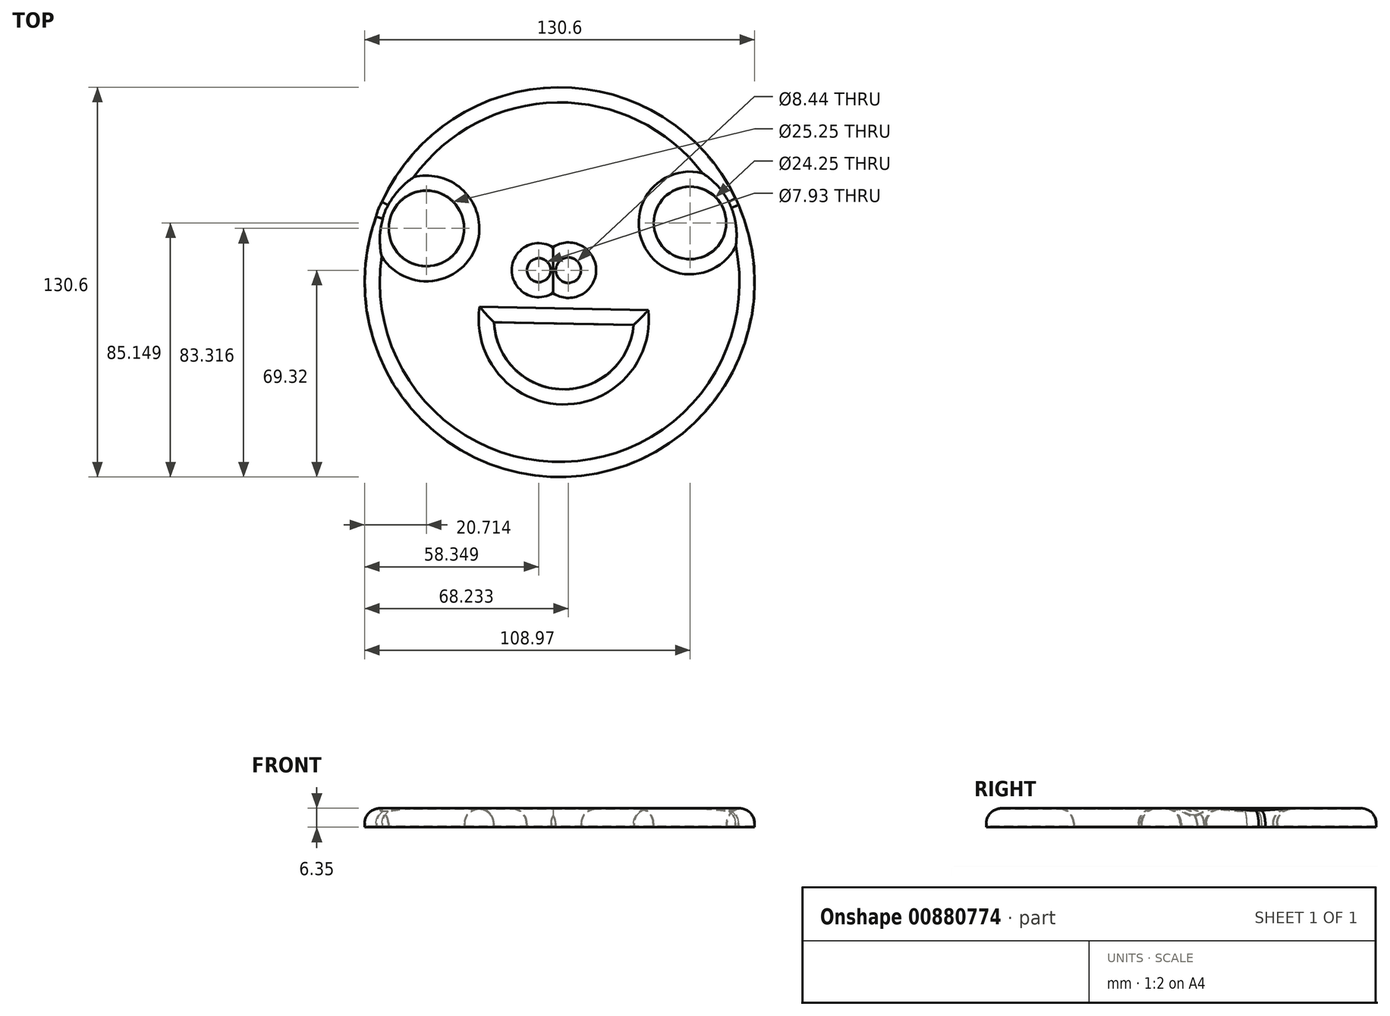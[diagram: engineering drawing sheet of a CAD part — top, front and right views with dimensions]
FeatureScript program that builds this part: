
annotation { "Feature Type Name" : "Feature", "Feature Type Description" : "" }
export const myFeature = defineFeature(function(context is Context, id is Id, definition is map)
    precondition{}
    {
        {
            var Q0;
            Q0=qCreatedBy(makeId("Top.planeOp"),FACE);
            var sketch = newSketch(context, id + "F0", { "sketchPlane" : qUnion([Q0])});
            skCircle(sketch, "E0", {"center": v(43.67, 24.89) * mm, "radius": 17.36 * mm});
            skCircle(sketch, "E1", {"center": v(-44.59, 23.06) * mm, "radius": 17.36 * mm});
            skCircle(sketch, "E2", {"center": v(-44.59, 23.06) * mm, "radius": 12.62 * mm});
            skCircle(sketch, "E3", {"center": v(43.67, 24.89) * mm, "radius": 12.12 * mm});
            skCircle(sketch, "E4", {"center": v(0, 5.04) * mm, "radius": 65.3 * mm});
            skArc(sketch, "E5", {"start": v(-21.99, -8.4) * mm, "mid": v(0.94, -30.84) * mm, "end": v(24.74, -9.31) * mm});
            skLineSegment(sketch, "E6", {"start": v(-21.99, -8.4) * mm, "end": v(24.74, -9.31) * mm});
            skCircle(sketch, "E7", {"center": v(-6.95, 9.06) * mm, "radius": 3.97 * mm});
            skCircle(sketch, "E8", {"center": v(2.93, 9.06) * mm, "radius": 4.22 * mm});
            skSolve(sketch);
        }
        {
            var Q0;
            Q0 = qSketchRegion(id + "F0", true);
            extrude(context, id + "F1", {"entities" : qUnion([Q0]), "depth" : 6.35 * mm, "offsetDistance" : 25.4 * mm});
        }
        {
            var Q0;
            Q0=makeQuery(id+"F1.opExtrude","CAP_FACE",FACE,{"disambiguationData":[OSD([sQuery(id+"F0.wireOp",EDGE,"E0"),sQuery(id+"F0.wireOp",EDGE,"E1"),sQuery(id+"F0.wireOp",EDGE,"E2"),sQuery(id+"F0.wireOp",EDGE,"E3"),sQuery(id+"F0.wireOp",EDGE,"E4"),sQuery(id+"F0.wireOp",EDGE,"E5"),sQuery(id+"F0.wireOp",EDGE,"E6")])],"isStart":false});
            fillet(context, id + "F2", {"entities" : qUnion([Q0]), "radius" : 5.08 * mm, "tangentPropagation" : true, "allowEdgeOverflow" : false});
        }
        {
            var Q0;
            Q0=makeQuery(id+"F1.opExtrude","CAP_FACE",FACE,{"disambiguationData":[OSD([sQuery(id+"F0.wireOp",EDGE,"E0"),sQuery(id+"F0.wireOp",EDGE,"E1"),sQuery(id+"F0.wireOp",EDGE,"E2"),sQuery(id+"F0.wireOp",EDGE,"E3"),sQuery(id+"F0.wireOp",EDGE,"E4"),sQuery(id+"F0.wireOp",EDGE,"E5"),sQuery(id+"F0.wireOp",EDGE,"E6")])],"isStart":false});
            shell(context, id + "F3", {"entities" : qUnion([Q0]), "thickness" : 0.25 * mm});
        }
    });
